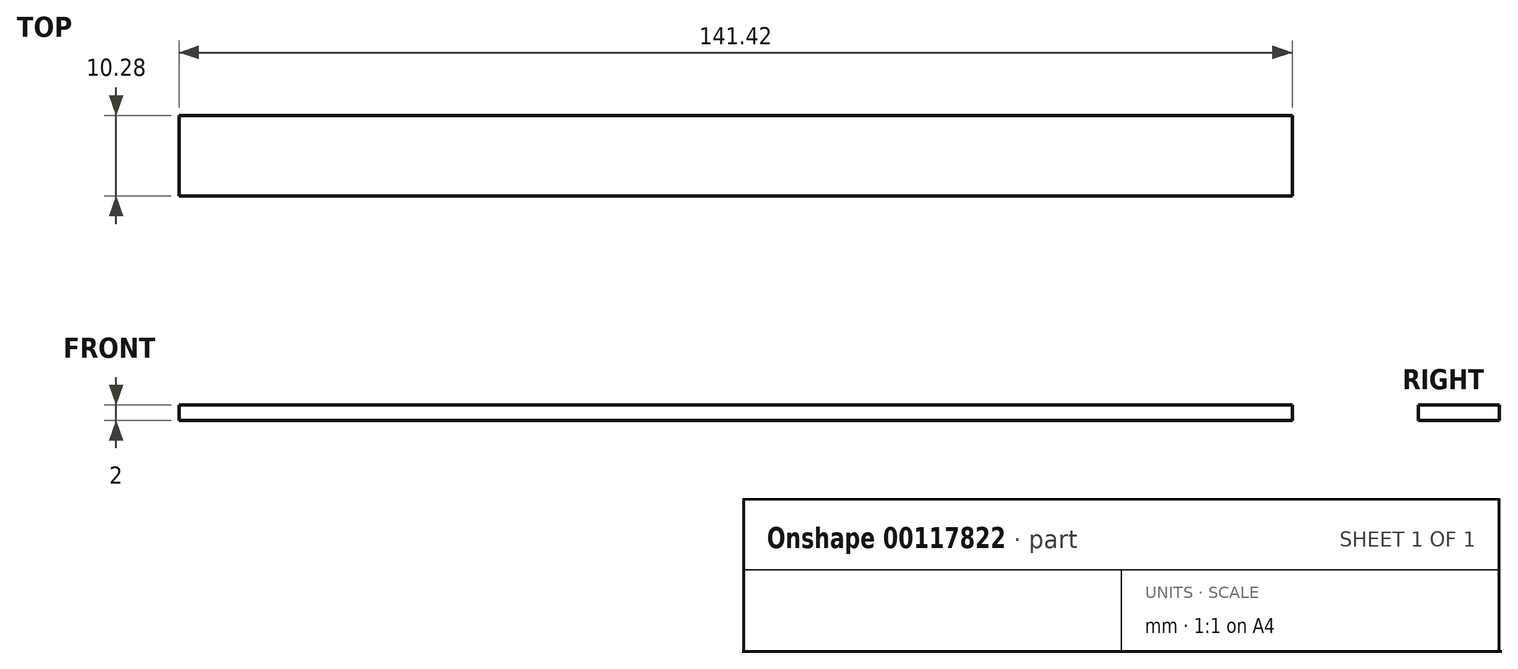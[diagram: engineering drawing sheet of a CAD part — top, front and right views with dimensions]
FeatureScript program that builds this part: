
annotation { "Feature Type Name" : "Feature", "Feature Type Description" : "" }
export const myFeature = defineFeature(function(context is Context, id is Id, definition is map)
    precondition{}
    {
        {
            var Q0;
            Q0=qCreatedBy(makeId("Top.planeOp"),FACE);
            var sketch = newSketch(context, id + "F0", { "sketchPlane" : qUnion([Q0])});
            skLineSegment(sketch, "E0.bottom", {"start": v(70.71, 5.14) * mm, "end": v(-70.71, 5.14) * mm});
            skLineSegment(sketch, "E0.top", {"start": v(70.71, -5.14) * mm, "end": v(-70.71, -5.14) * mm});
            skLineSegment(sketch, "E0.left", {"start": v(70.71, 5.14) * mm, "end": v(70.71, -5.14) * mm});
            skLineSegment(sketch, "E0.right", {"start": v(-70.71, 5.14) * mm, "end": v(-70.71, -5.14) * mm});
            skPoint(sketch, "E0.middle", {"position": v(0, 0) * mm});
            skSolve(sketch);
        }
        {
            var Q0;
            Q0=makeQuery(id+"F0.imprint","IMPRINT",FACE,{"disambiguationData":[TD([[makeQuery(id+"F0.imprint","IMPRINT",EDGE,{"derivedFrom":sQuery(id+"F0.wireOp",EDGE,"E0.bottom")}),1.0]])]});
            extrude(context, id + "F1", {"entities" : qUnion([Q0]), "depth" : 2 * mm});
        }
    });
